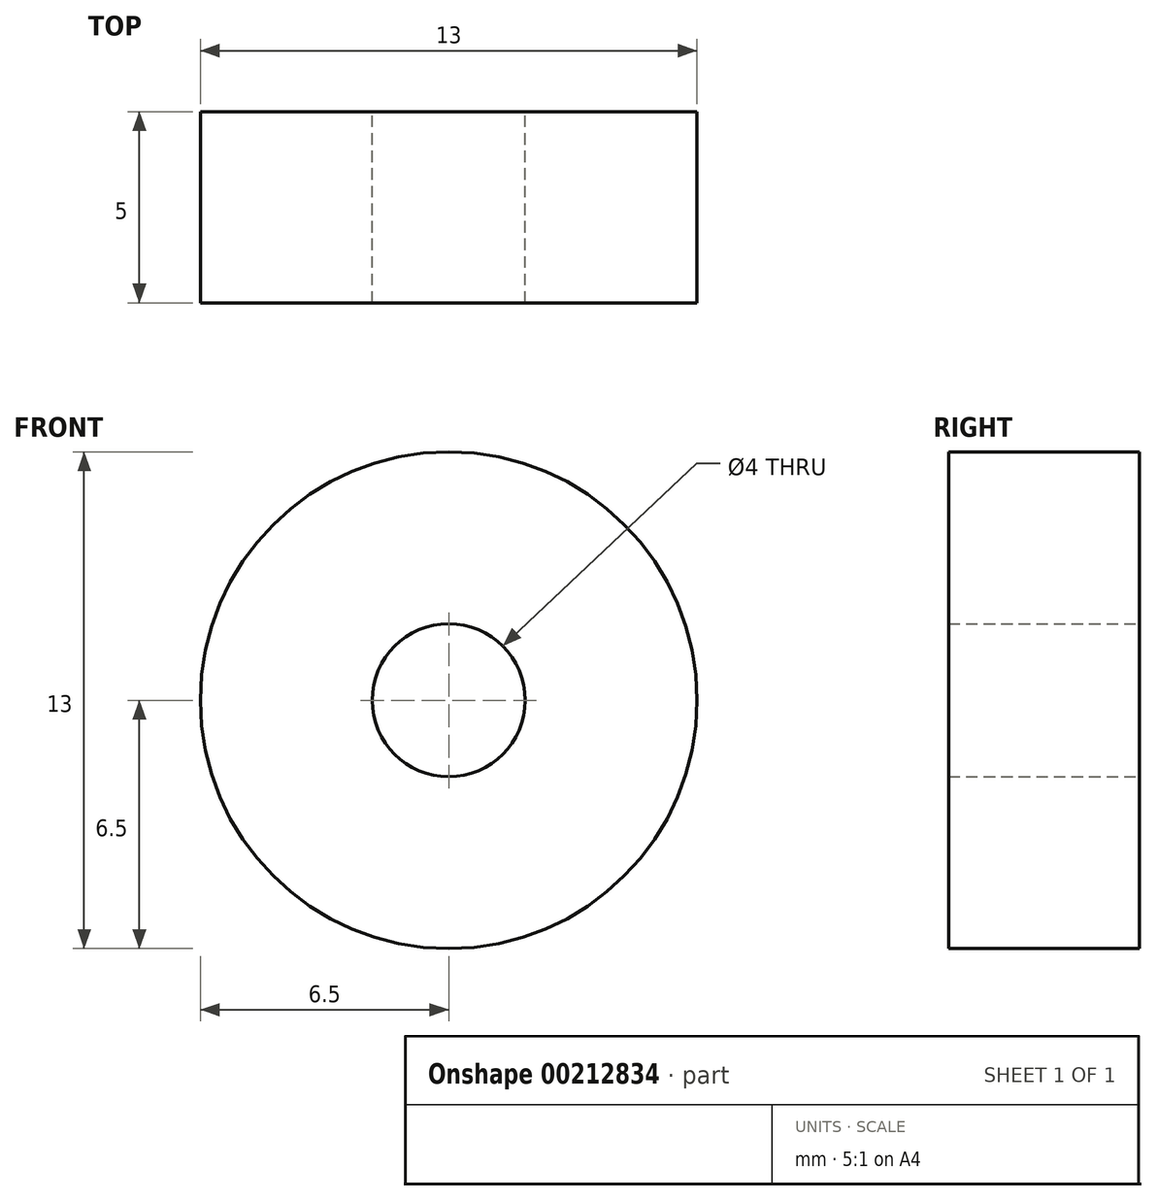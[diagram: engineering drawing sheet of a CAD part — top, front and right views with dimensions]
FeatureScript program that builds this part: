
annotation { "Feature Type Name" : "Feature", "Feature Type Description" : "" }
export const myFeature = defineFeature(function(context is Context, id is Id, definition is map)
    precondition{}
    {
        {
            var Q0;
            Q0=qCreatedBy(makeId("Front.planeOp"),FACE);
            var sketch = newSketch(context, id + "F0", { "sketchPlane" : qUnion([Q0])});
            skCircle(sketch, "E0", {"center": v(0, 0) * mm, "radius": 2 * mm});
            skCircle(sketch, "E1", {"center": v(0, 0) * mm, "radius": 6.5 * mm});
            skSolve(sketch);
        }
        {
            var Q0;
            Q0=qSketchRegion(id+"F0",true);
            extrude(context, id + "F1", {"entities" : qUnion([Q0]), "depth" : 5 * mm});
        }
    });
